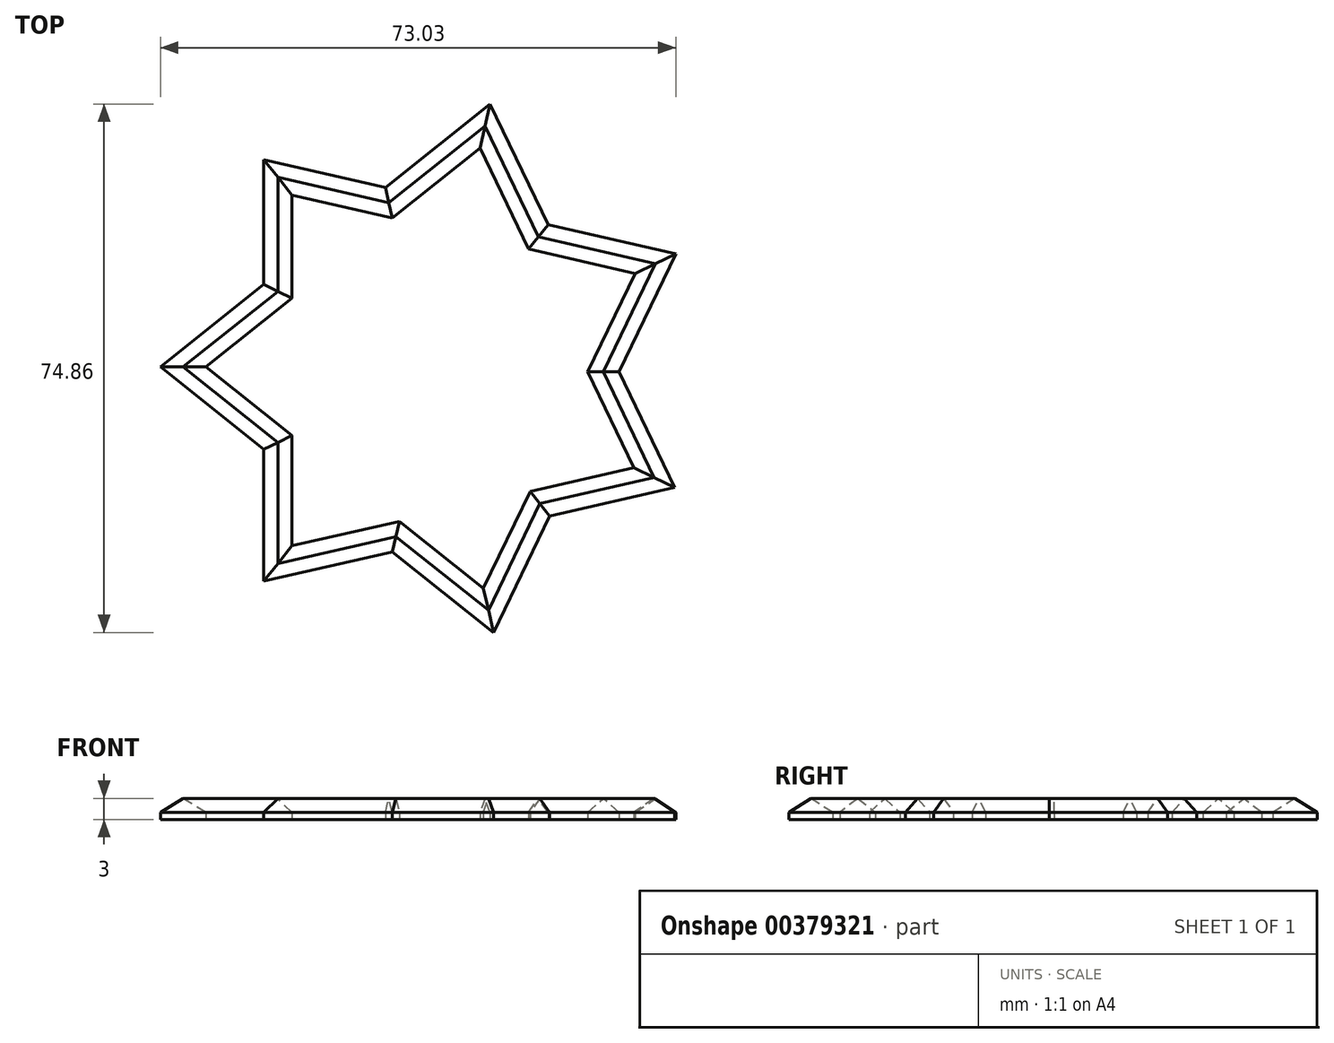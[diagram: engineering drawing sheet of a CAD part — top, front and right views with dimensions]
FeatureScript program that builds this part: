
annotation { "Feature Type Name" : "Feature", "Feature Type Description" : "" }
export const myFeature = defineFeature(function(context is Context, id is Id, definition is map)
    precondition{}
    {
        {
            var Q0;
            Q0=qCreatedBy(makeId("Top.planeOp"),FACE);
            var sketch = newSketch(context, id + "F0", { "sketchPlane" : qUnion([Q0])});
            skPoint(sketch, "E0.0.midPoint", {"position": v(24.09, -0.53) * mm});
            skLineSegment(sketch, "E1", {"start": v(-2.16, 37.23) * mm, "end": v(6.07, 20.15) * mm});
            skLineSegment(sketch, "E2", {"start": v(-34.22, -30.37) * mm, "end": v(-15.98, -26.2) * mm});
            skLineSegment(sketch, "E3", {"start": v(-34.22, -30.37) * mm, "end": v(-34.22, -11.66) * mm});
            skLineSegment(sketch, "E4", {"start": v(-34.22, 29.35) * mm, "end": v(-16.98, 25.41) * mm});
            skLineSegment(sketch, "E5", {"start": v(24.18, 16.02) * mm, "end": v(16.12, -0.72) * mm});
            skLineSegment(sketch, "E6", {"start": v(-1.66, -37.63) * mm, "end": v(-15.98, -26.2) * mm});
            skLineSegment(sketch, "E7", {"start": v(-48.85, 0) * mm, "end": v(-34.22, 11.66) * mm});
            skLineSegment(sketch, "E8.trimOffspring", {"start": v(-16.98, 25.41) * mm, "end": v(-2.16, 37.23) * mm});
            skLineSegment(sketch, "E9.trimOffspring", {"start": v(6.07, 20.15) * mm, "end": v(24.18, 16.02) * mm});
            skLineSegment(sketch, "E10.trimOffspring", {"start": v(16.12, -0.72) * mm, "end": v(24, -17.08) * mm});
            skLineSegment(sketch, "E11.trimOffspring", {"start": v(6.3, -21.13) * mm, "end": v(-1.66, -37.63) * mm});
            skLineSegment(sketch, "E12.trimOffspring", {"start": v(6.3, -21.13) * mm, "end": v(24, -17.08) * mm});
            skLineSegment(sketch, "E13.trimOffspring", {"start": v(-34.22, -11.66) * mm, "end": v(-48.85, 0) * mm});
            skLineSegment(sketch, "E14.trimOffspring", {"start": v(-34.22, 11.66) * mm, "end": v(-34.22, 29.35) * mm});
            skLineSegment(sketch, "E15.0", {"start": v(-30.22, 9.74) * mm, "end": v(-30.22, 24.33) * mm});
            skLineSegment(sketch, "E15.1", {"start": v(-42.43, 0) * mm, "end": v(-30.22, 9.74) * mm});
            skLineSegment(sketch, "E15.2", {"start": v(-30.22, -9.74) * mm, "end": v(-42.43, 0) * mm});
            skLineSegment(sketch, "E15.3", {"start": v(18.4, 13.23) * mm, "end": v(11.68, -0.72) * mm});
            skLineSegment(sketch, "E15.4", {"start": v(3.3, 16.68) * mm, "end": v(18.4, 13.23) * mm});
            skLineSegment(sketch, "E15.5", {"start": v(-3.59, 30.98) * mm, "end": v(3.3, 16.68) * mm});
            skLineSegment(sketch, "E15.6", {"start": v(-16, 21.08) * mm, "end": v(-3.59, 30.98) * mm});
            skLineSegment(sketch, "E15.7", {"start": v(11.68, -0.72) * mm, "end": v(18.22, -14.3) * mm});
            skLineSegment(sketch, "E15.8", {"start": v(3.52, -17.65) * mm, "end": v(18.22, -14.3) * mm});
            skLineSegment(sketch, "E15.9", {"start": v(3.52, -17.65) * mm, "end": v(-3.09, -31.38) * mm});
            skLineSegment(sketch, "E15.10", {"start": v(-30.22, 24.33) * mm, "end": v(-16, 21.08) * mm});
            skLineSegment(sketch, "E15.11", {"start": v(-3.09, -31.38) * mm, "end": v(-15, -21.88) * mm});
            skLineSegment(sketch, "E15.12", {"start": v(-30.22, -25.36) * mm, "end": v(-15, -21.88) * mm});
            skLineSegment(sketch, "E15.13", {"start": v(-30.22, -25.36) * mm, "end": v(-30.22, -9.74) * mm});
            skSolve(sketch);
        }
        {
            var Q0;
            Q0=makeQuery(id+"F0.imprint","IMPRINT",FACE,{"disambiguationData":[TD([[makeQuery(id+"F0.imprint","IMPRINT",EDGE,{"derivedFrom":sQuery(id+"F0.wireOp",EDGE,"E1")}),-1.0]])]});
            extrude(context, id + "F1", {"entities" : qUnion([Q0]), "depth" : 3 * mm});
        }
        {
            var Q0;
            Q0=makeQuery(id+"F1.opExtrude","CAP_FACE",FACE,{"disambiguationData":[OSD([sQuery(id+"F0.wireOp",EDGE,"E1"),sQuery(id+"F0.wireOp",EDGE,"E2"),sQuery(id+"F0.wireOp",EDGE,"E3"),sQuery(id+"F0.wireOp",EDGE,"E4"),sQuery(id+"F0.wireOp",EDGE,"E5"),sQuery(id+"F0.wireOp",EDGE,"E6"),sQuery(id+"F0.wireOp",EDGE,"E7"),sQuery(id+"F0.wireOp",EDGE,"E8.trimOffspring"),sQuery(id+"F0.wireOp",EDGE,"E9.trimOffspring"),sQuery(id+"F0.wireOp",EDGE,"E10.trimOffspring"),sQuery(id+"F0.wireOp",EDGE,"E11.trimOffspring"),sQuery(id+"F0.wireOp",EDGE,"E12.trimOffspring"),sQuery(id+"F0.wireOp",EDGE,"E13.trimOffspring"),sQuery(id+"F0.wireOp",EDGE,"E14.trimOffspring"),sQuery(id+"F0.wireOp",EDGE,"E15.0"),sQuery(id+"F0.wireOp",EDGE,"E15.1"),sQuery(id+"F0.wireOp",EDGE,"E15.2"),sQuery(id+"F0.wireOp",EDGE,"E15.3"),sQuery(id+"F0.wireOp",EDGE,"E15.4"),sQuery(id+"F0.wireOp",EDGE,"E15.5"),sQuery(id+"F0.wireOp",EDGE,"E15.6"),sQuery(id+"F0.wireOp",EDGE,"E15.7"),sQuery(id+"F0.wireOp",EDGE,"E15.8"),sQuery(id+"F0.wireOp",EDGE,"E15.9"),sQuery(id+"F0.wireOp",EDGE,"E15.10"),sQuery(id+"F0.wireOp",EDGE,"E15.11"),sQuery(id+"F0.wireOp",EDGE,"E15.12"),sQuery(id+"F0.wireOp",EDGE,"E15.13")])],"isStart":false});
            chamfer(context, id + "F2", {"entities" : qUnion([Q0]), "width" : 2 * mm, "tangentPropagation" : true});
        }
    });
